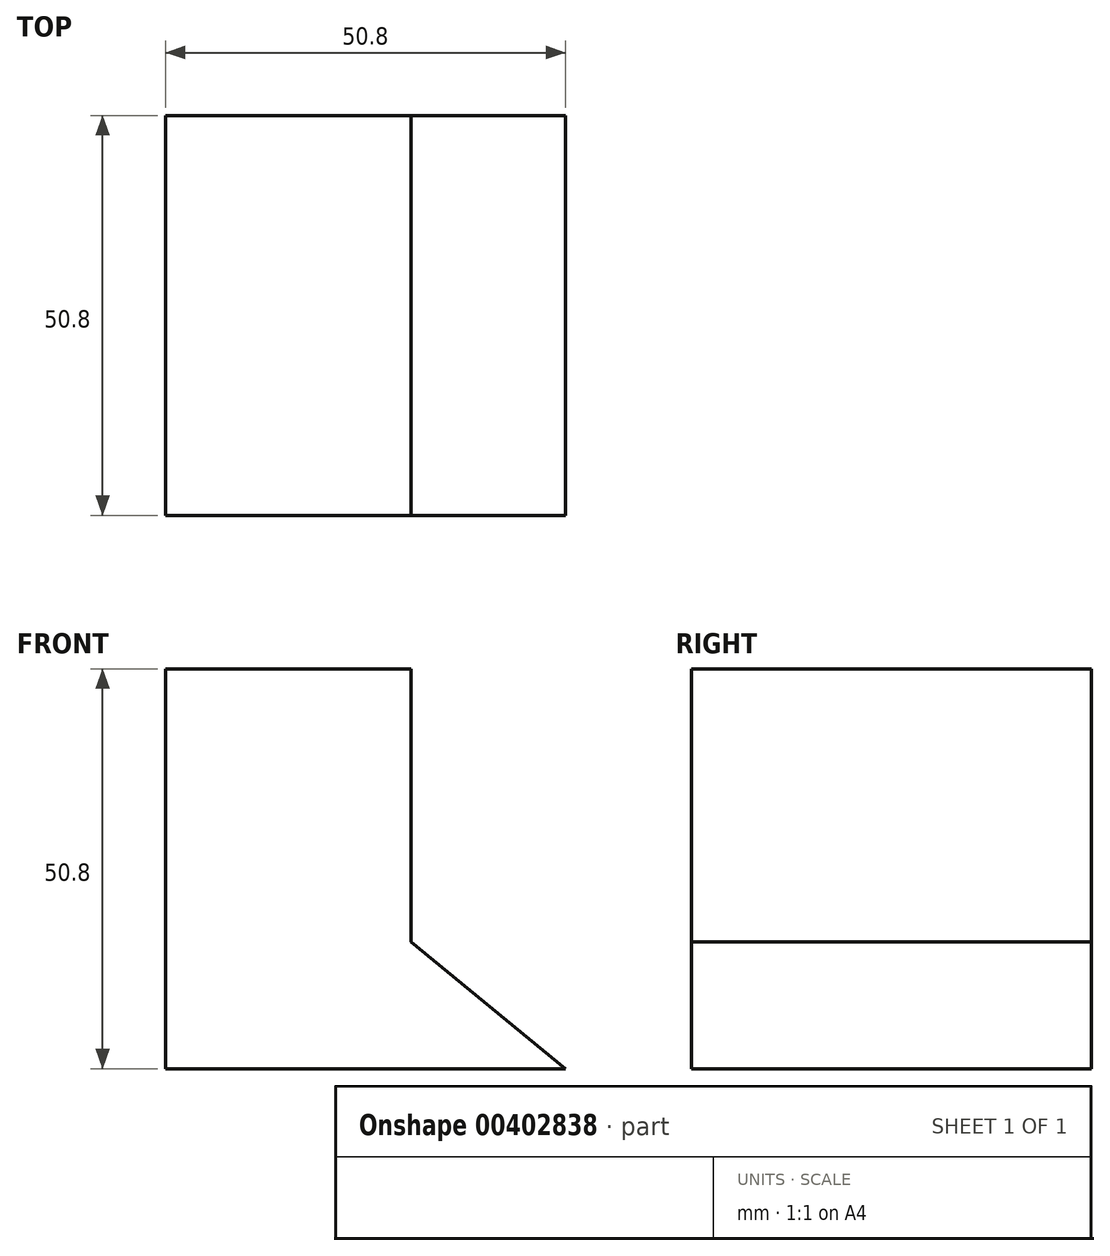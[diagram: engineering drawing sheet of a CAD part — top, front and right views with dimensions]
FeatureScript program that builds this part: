
annotation { "Feature Type Name" : "Feature", "Feature Type Description" : "" }
export const myFeature = defineFeature(function(context is Context, id is Id, definition is map)
    precondition{}
    {
        {
            var Q0;
            Q0=qCreatedBy(makeId("Front.planeOp"),FACE);
            var sketch = newSketch(context, id + "F0", { "sketchPlane" : qUnion([Q0])});
            skLineSegment(sketch, "E0", {"start": v(0, 0) * mm, "end": v(0, 50.8) * mm});
            skLineSegment(sketch, "E1", {"start": v(0, 0) * mm, "end": v(50.8, 0) * mm});
            skLineSegment(sketch, "E2", {"start": v(50.8, 0) * mm, "end": v(31.16, 16.1) * mm});
            skLineSegment(sketch, "E3", {"start": v(0, 50.8) * mm, "end": v(29.34, 50.8) * mm});
            skLineSegment(sketch, "E4", {"start": v(31.16, 16.1) * mm, "end": v(31.16, 50.8) * mm});
            skLineSegment(sketch, "E5", {"start": v(29.34, 50.8) * mm, "end": v(31.16, 50.8) * mm});
            skSolve(sketch);
        }
        {
            var Q0;
            Q0=makeQuery(id+"F0.imprint","IMPRINT",FACE,{"disambiguationData":[TD([[makeQuery(id+"F0.imprint","IMPRINT",EDGE,{"derivedFrom":sQuery(id+"F0.wireOp",EDGE,"E0")}),-1.0]])]});
            extrude(context, id + "F1", {"entities" : qUnion([Q0]), "depth" : 50.8 * mm});
        }
    });
